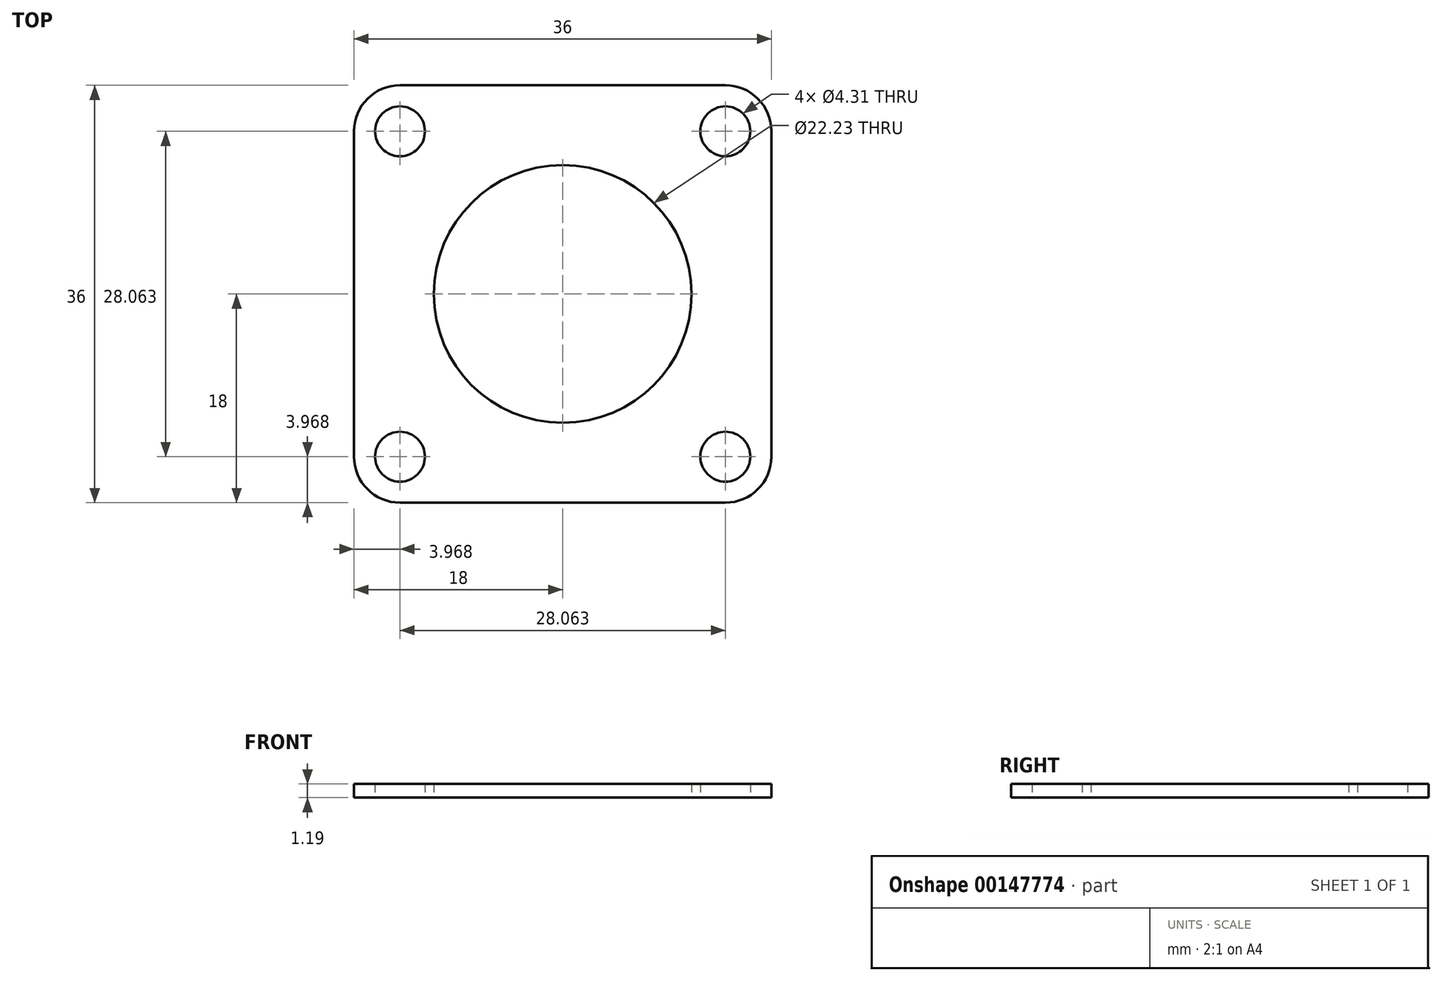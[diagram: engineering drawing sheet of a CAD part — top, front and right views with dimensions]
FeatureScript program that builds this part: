
annotation { "Feature Type Name" : "Feature", "Feature Type Description" : "" }
export const myFeature = defineFeature(function(context is Context, id is Id, definition is map)
    precondition{}
    {
        {
            var Q0;
            Q0=qCreatedBy(makeId("Top.planeOp"),FACE);
            var sketch = newSketch(context, id + "F0", { "sketchPlane" : qUnion([Q0])});
            skCircle(sketch, "E0", {"center": v(0, 0) * mm, "radius": 11.11 * mm});
            skLineSegment(sketch, "E1.bottom", {"start": v(14.03, 14.03) * mm, "end": v(-14.03, 14.03) * mm, "construction": true});
            skLineSegment(sketch, "E1.top", {"start": v(14.03, -14.03) * mm, "end": v(-14.03, -14.03) * mm, "construction": true});
            skLineSegment(sketch, "E1.left", {"start": v(14.03, 14.03) * mm, "end": v(14.03, -14.03) * mm, "construction": true});
            skLineSegment(sketch, "E1.right", {"start": v(-14.03, 14.03) * mm, "end": v(-14.03, -14.03) * mm, "construction": true});
            skCircle(sketch, "E2", {"center": v(-14.03, 14.03) * mm, "radius": 3.97 * mm, "construction": true});
            skCircle(sketch, "E3", {"center": v(-14.03, 14.03) * mm, "radius": 2.15 * mm});
            skCircle(sketch, "E4", {"center": v(-14.03, -14.03) * mm, "radius": 2.15 * mm});
            skCircle(sketch, "E5", {"center": v(14.03, -14.03) * mm, "radius": 2.15 * mm});
            skCircle(sketch, "E6", {"center": v(14.03, 14.03) * mm, "radius": 2.15 * mm});
            skLineSegment(sketch, "E7.bottom", {"start": v(18, 18) * mm, "end": v(-18, 18) * mm});
            skLineSegment(sketch, "E7.top", {"start": v(18, -18) * mm, "end": v(-18, -18) * mm});
            skLineSegment(sketch, "E7.left", {"start": v(18, 18) * mm, "end": v(18, -18) * mm});
            skLineSegment(sketch, "E7.right", {"start": v(-18, 18) * mm, "end": v(-18, -18) * mm});
            skSolve(sketch);
        }
        {
            var Q0;
            Q0=qSketchRegion(id+"F0",true);
            extrude(context, id + "F1", {"entities" : qUnion([Q0]), "depth" : 1.2 * mm});
        }
        {
            var Q0;
            Q0=makeQuery(id+"F1.opExtrude","SWEPT_EDGE",EDGE,{"disambiguationData":[OSD([sQuery(id+"F0.wireOp",EDGE,"E7.top"),sQuery(id+"F0.wireOp",EDGE,"E7.right")])]});
            var Q1;
            Q1=makeQuery(id+"F1.opExtrude","SWEPT_EDGE",EDGE,{"disambiguationData":[OSD([sQuery(id+"F0.wireOp",EDGE,"E7.top"),sQuery(id+"F0.wireOp",EDGE,"E7.left")])]});
            var Q2;
            Q2=makeQuery(id+"F1.opExtrude","SWEPT_EDGE",EDGE,{"disambiguationData":[OSD([sQuery(id+"F0.wireOp",EDGE,"E7.bottom"),sQuery(id+"F0.wireOp",EDGE,"E7.left")])]});
            var Q3;
            Q3=makeQuery(id+"F1.opExtrude","SWEPT_EDGE",EDGE,{"disambiguationData":[OSD([sQuery(id+"F0.wireOp",EDGE,"E7.bottom"),sQuery(id+"F0.wireOp",EDGE,"E7.right")])]});
            fillet(context, id + "F2", {"entities" : qUnion([Q0, Q1, Q2, Q3]), "radius" : 3.97 * mm, "tangentPropagation" : true, "allowEdgeOverflow" : false});
        }
    });
